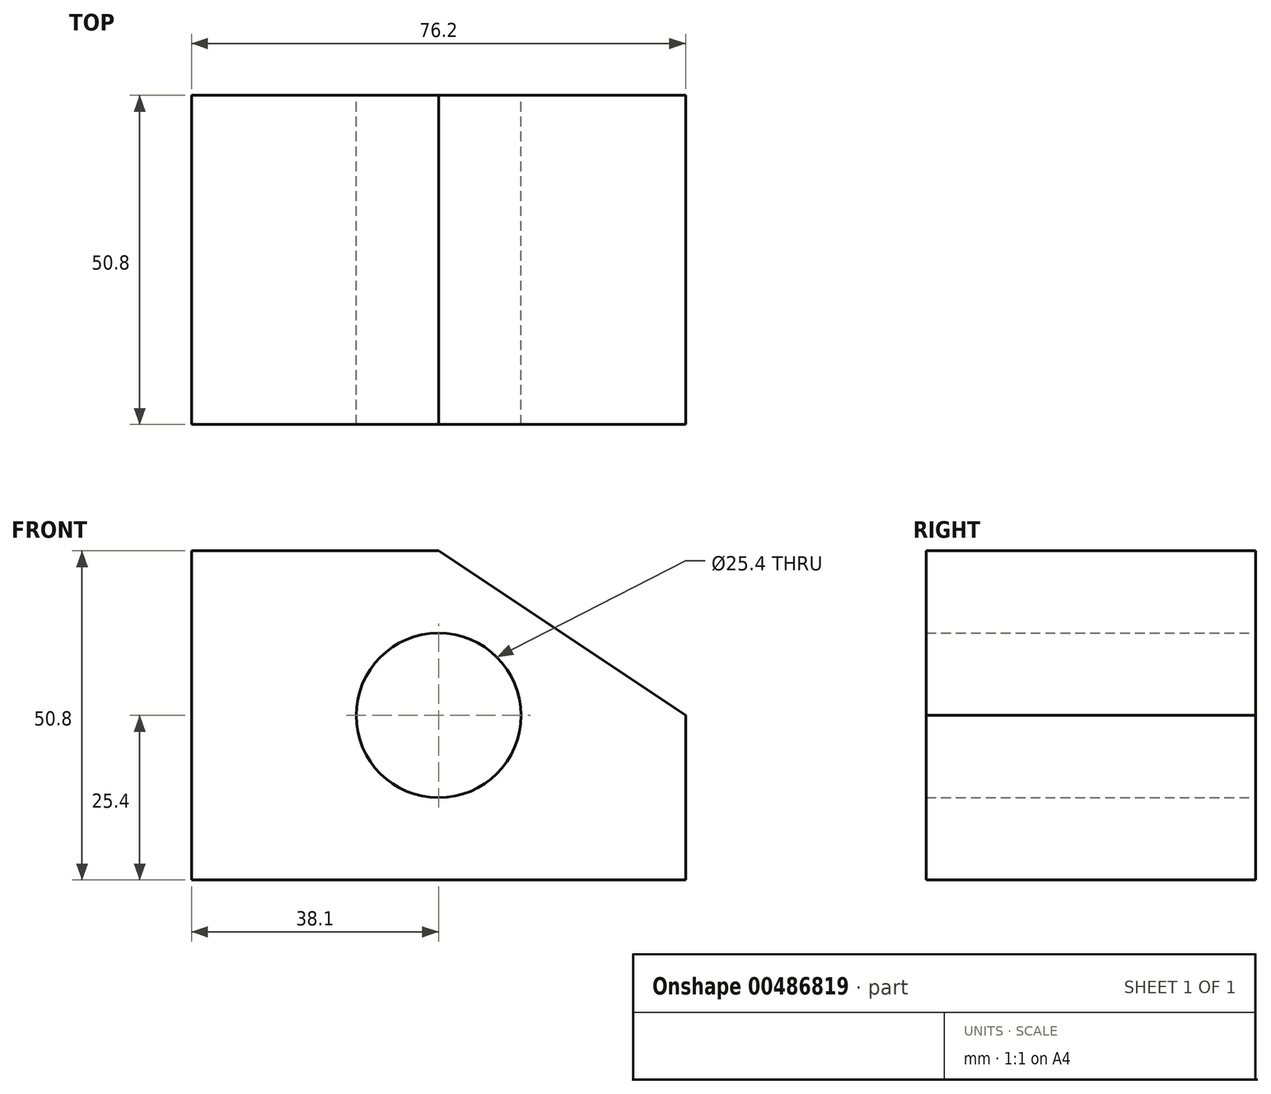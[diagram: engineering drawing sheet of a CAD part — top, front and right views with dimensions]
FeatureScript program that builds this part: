
annotation { "Feature Type Name" : "Feature", "Feature Type Description" : "" }
export const myFeature = defineFeature(function(context is Context, id is Id, definition is map)
    precondition{}
    {
        {
            var Q0;
            Q0=qCreatedBy(makeId("Front.planeOp"),FACE);
            var sketch = newSketch(context, id + "F0", { "sketchPlane" : qUnion([Q0])});
            skLineSegment(sketch, "E0.bottom", {"start": v(0, 0) * mm, "end": v(76.2, 0) * mm});
            skLineSegment(sketch, "E0.top", {"start": v(0, 50.8) * mm, "end": v(76.2, 50.8) * mm});
            skLineSegment(sketch, "E0.left", {"start": v(0, 0) * mm, "end": v(0, 50.8) * mm});
            skLineSegment(sketch, "E0.right", {"start": v(76.2, 0) * mm, "end": v(76.2, 50.8) * mm});
            skLineSegment(sketch, "E1.top", {"start": v(0, 0) * mm, "end": v(38.1, 0) * mm});
            skLineSegment(sketch, "E1.left", {"start": v(0, 25.4) * mm, "end": v(0, 0) * mm});
            skCircle(sketch, "E2", {"center": v(38.1, 25.4) * mm, "radius": 12.7 * mm});
            skLineSegment(sketch, "E3", {"start": v(76.2, 25.4) * mm, "end": v(38.1, 50.8) * mm});
            skSolve(sketch);
        }
        {
            var Q0;
            Q0 = qSketchRegion(id + "F0", true);
            extrude(context, id + "F1", {"entities" : qUnion([Q0]), "depth" : 50.8 * mm});
        }
        {
            var Q0;
            {var subQ3=sQuery(id+"F0.wireOp",EDGE,"E3");Q0=makeQuery(id+"F0.imprint","IMPRINT",FACE,{"disambiguationData":[TD([[makeQuery(id+"F0.imprint","IMPRINT",EDGE,{"derivedFrom":subQ3}),-1.0]])]});}
            extrude(context, id + "F2", {"entities" : qUnion([Q0]), "operationType" : NewBodyOperationType.REMOVE, "depth" : 50.8 * mm});
        }
    });
